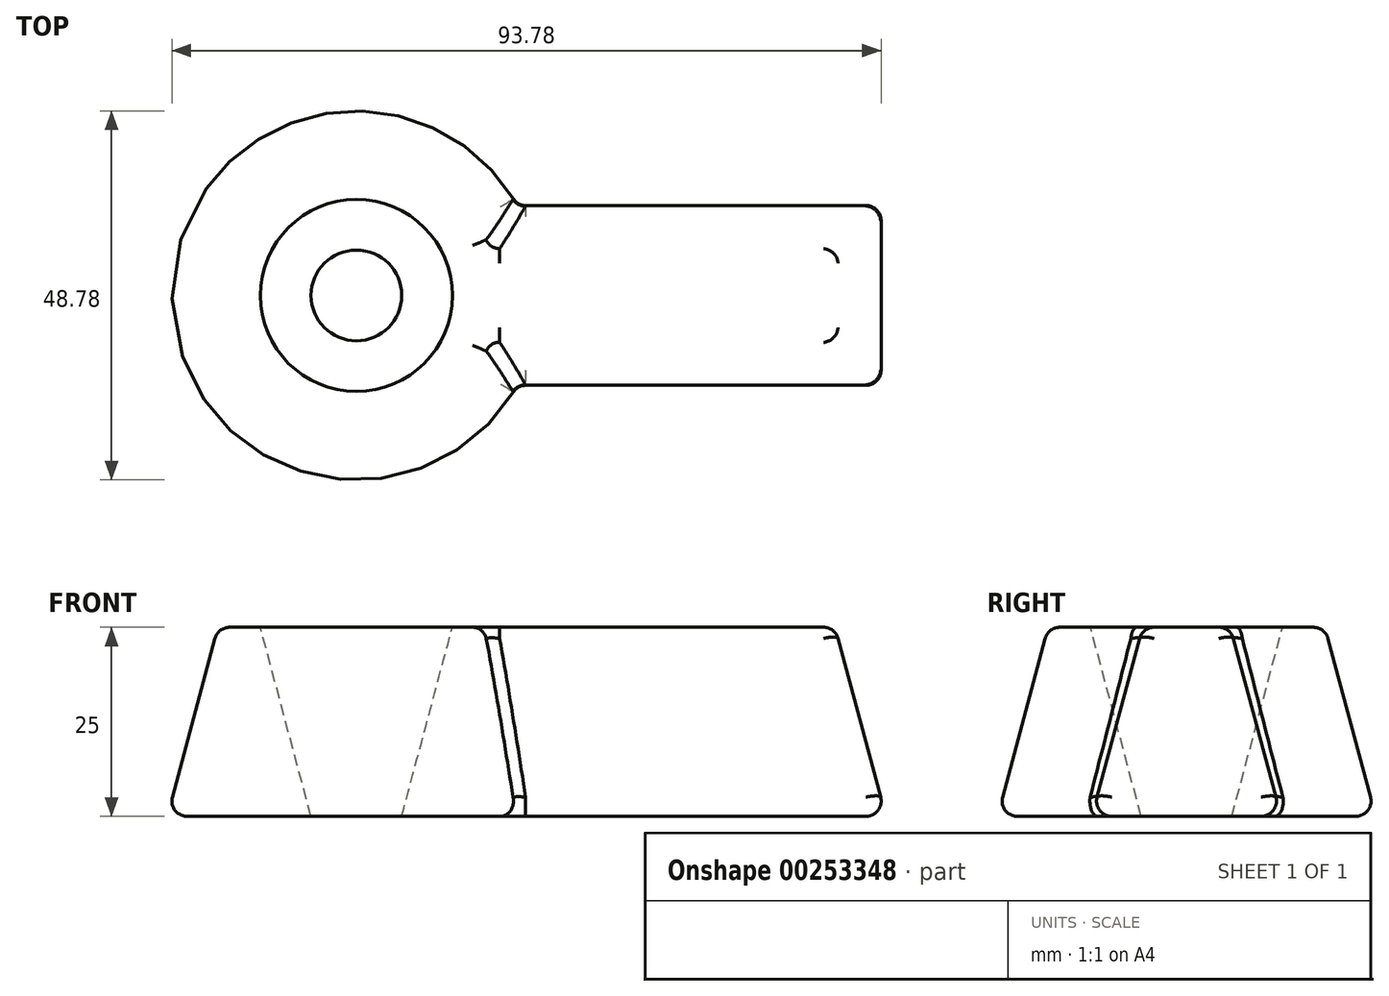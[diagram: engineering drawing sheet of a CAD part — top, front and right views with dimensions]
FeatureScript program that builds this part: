
annotation { "Feature Type Name" : "Feature", "Feature Type Description" : "" }
export const myFeature = defineFeature(function(context is Context, id is Id, definition is map)
    precondition{}
    {
        {
            var Q0;
            Q0=qCreatedBy(makeId("Top.planeOp"),FACE);
            var sketch = newSketch(context, id + "F0", { "sketchPlane" : qUnion([Q0])});
            skCircle(sketch, "E0", {"center": v(0, 0) * mm, "radius": 25 * mm});
            skLineSegment(sketch, "E1.bottom", {"start": v(0, 12.5) * mm, "end": v(70, 12.5) * mm});
            skLineSegment(sketch, "E1.top", {"start": v(0, -12.5) * mm, "end": v(70, -12.5) * mm});
            skLineSegment(sketch, "E1.left", {"start": v(0, 12.5) * mm, "end": v(0, -12.5) * mm});
            skLineSegment(sketch, "E1.right", {"start": v(70, 12.5) * mm, "end": v(70, -12.5) * mm});
            skCircle(sketch, "E2", {"center": v(0, 0) * mm, "radius": 6 * mm});
            skSolve(sketch);
        }
        {
            var Q0;
            Q0 = qSketchRegion(id + "F0", true);
            extrude(context, id + "F1", {"entities" : qUnion([Q0]), "depth" : 25 * mm, "hasDraft" : true, "draftAngle" : 15 * degree, "draftPullDirection" : true});
        }
        {
            var Q0;
            Q0=makeQuery(id+"F1.opExtrude","SWEPT_EDGE",EDGE,{"disambiguationData":[OSD([sQuery(id+"F0.wireOp",EDGE,"E0"),sQuery(id+"F0.wireOp",EDGE,"E1.top")])]});
            var Q1;
            Q1=makeQuery(id+"F1.opExtrude","SWEPT_EDGE",EDGE,{"disambiguationData":[OSD([sQuery(id+"F0.wireOp",EDGE,"E0"),sQuery(id+"F0.wireOp",EDGE,"E1.bottom")])]});
            var Q2;
            Q2=makeQuery(id+"F1.opExtrude","SWEPT_EDGE",EDGE,{"disambiguationData":[OSD([sQuery(id+"F0.wireOp",EDGE,"E1.bottom"),sQuery(id+"F0.wireOp",EDGE,"E1.right")])]});
            var Q3;
            Q3=makeQuery(id+"F1.opExtrude","SWEPT_EDGE",EDGE,{"disambiguationData":[OSD([sQuery(id+"F0.wireOp",EDGE,"E1.top"),sQuery(id+"F0.wireOp",EDGE,"E1.right")])]});
            fillet(context, id + "F2", {"entities" : qUnion([Q0, Q1, Q2, Q3]), "radius" : 2 * mm, "tangentPropagation" : true, "allowEdgeOverflow" : false});
        }
        {
            var Q0;
            Q0=makeQuery(id+"F1.opExtrude","CAP_EDGE",EDGE,{"disambiguationData":[OSD([sQuery(id+"F0.wireOp",EDGE,"E1.bottom")])],"isStart":false});
            var Q1;
            Q1=makeQuery(id+"F1.opExtrude","CAP_EDGE",EDGE,{"disambiguationData":[OSD([sQuery(id+"F0.wireOp",EDGE,"E1.bottom")])],"isStart":true});
            fillet(context, id + "F3", {"entities" : qUnion([Q0, Q1]), "radius" : 2 * mm, "tangentPropagation" : true, "allowEdgeOverflow" : false});
        }
    });
